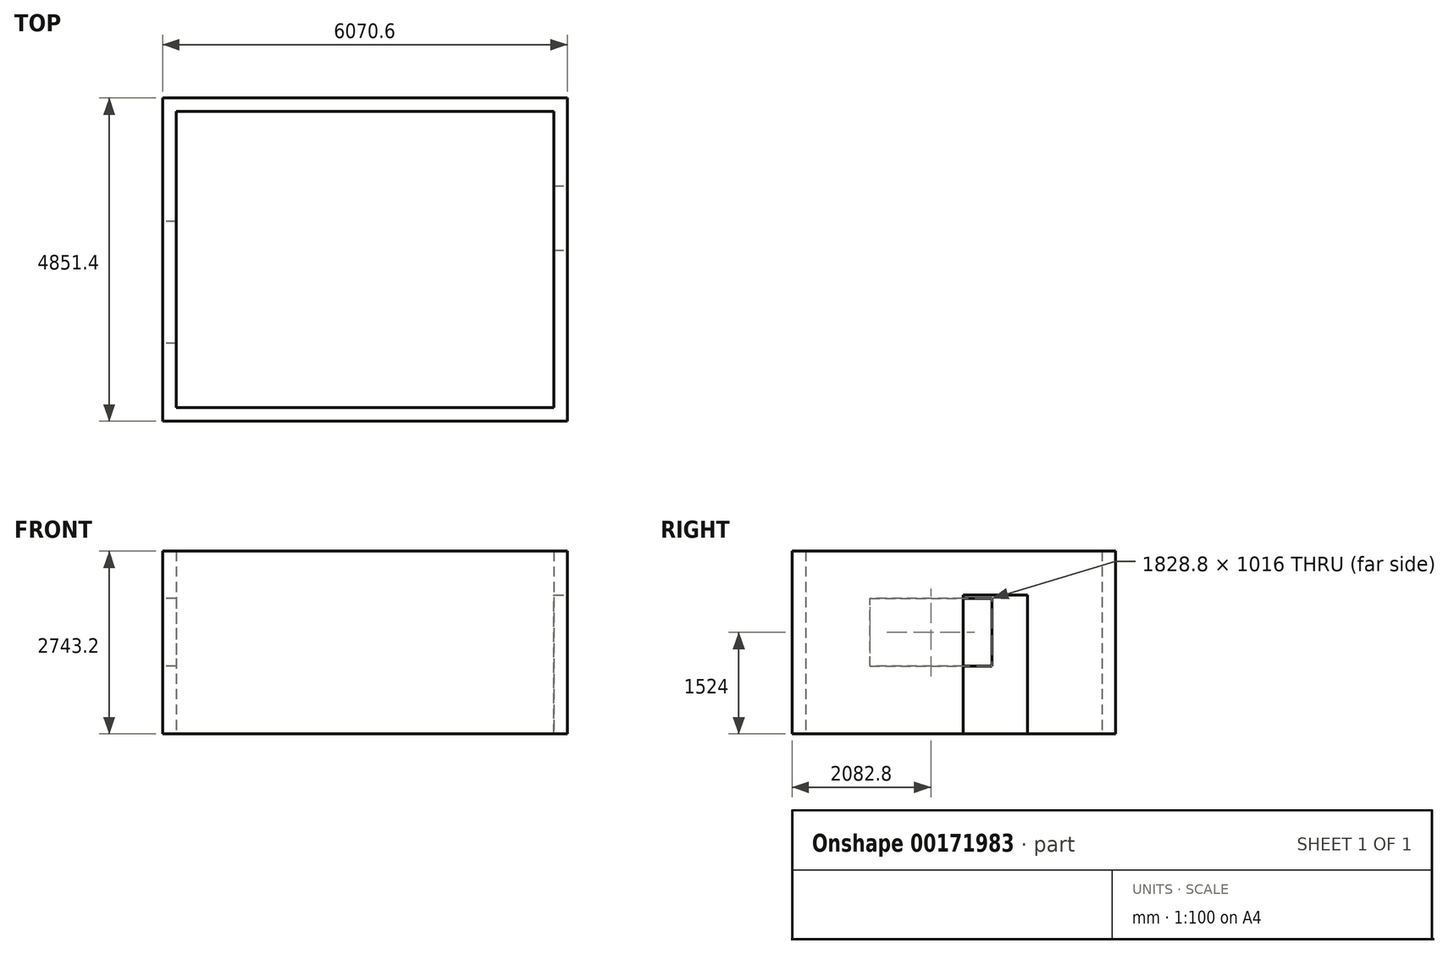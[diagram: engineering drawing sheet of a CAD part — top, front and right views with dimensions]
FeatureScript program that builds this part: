
annotation { "Feature Type Name" : "Feature", "Feature Type Description" : "" }
export const myFeature = defineFeature(function(context is Context, id is Id, definition is map)
    precondition{}
    {
        {
            var Q0;
            Q0=qCreatedBy(makeId("Top.planeOp"),FACE);
            var sketch = newSketch(context, id + "F0", { "sketchPlane" : qUnion([Q0])});
            skLineSegment(sketch, "E0.bottom", {"start": v(3035.3, 2425.7) * mm, "end": v(-3035.3, 2425.7) * mm});
            skLineSegment(sketch, "E0.top", {"start": v(3035.3, -2425.7) * mm, "end": v(-3035.3, -2425.7) * mm});
            skLineSegment(sketch, "E0.left", {"start": v(3035.3, 2425.7) * mm, "end": v(3035.3, -2425.7) * mm});
            skLineSegment(sketch, "E0.right", {"start": v(-3035.3, 2425.7) * mm, "end": v(-3035.3, -2425.7) * mm});
            skPoint(sketch, "E0.middle", {"position": v(0, 0) * mm});
            skLineSegment(sketch, "E1.bottom", {"start": v(2832.1, 2222.5) * mm, "end": v(-2832.1, 2222.5) * mm});
            skLineSegment(sketch, "E1.top", {"start": v(2832.1, -2222.5) * mm, "end": v(-2832.1, -2222.5) * mm});
            skLineSegment(sketch, "E1.left", {"start": v(2832.1, 2222.5) * mm, "end": v(2832.1, -2222.5) * mm});
            skLineSegment(sketch, "E1.right", {"start": v(-2832.1, 2222.5) * mm, "end": v(-2832.1, -2222.5) * mm});
            skSolve(sketch);
        }
        {
            var Q0;
            Q0 = qSketchRegion(id + "F0", true);
            extrude(context, id + "F1", {"entities" : qUnion([Q0]), "depth" : 2438.4 * mm});
        }
        {
            var Q0;
            Q0=makeQuery(id+"F1.opExtrude","SWEPT_FACE",FACE,{"disambiguationData":[OSD([sQuery(id+"F0.wireOp",EDGE,"E0.right")])]});
            var sketch = newSketch(context, id + "F2", { "sketchPlane" : qUnion([Q0])});
            skLineSegment(sketch, "E2.bottom", {"start": v(1257.3, 1016) * mm, "end": v(-571.5, 1016) * mm});
            skLineSegment(sketch, "E2.top", {"start": v(1257.3, 2032) * mm, "end": v(-571.5, 2032) * mm});
            skLineSegment(sketch, "E2.left", {"start": v(1257.3, 1016) * mm, "end": v(1257.3, 2032) * mm});
            skLineSegment(sketch, "E2.right", {"start": v(-571.5, 1016) * mm, "end": v(-571.5, 2032) * mm});
            skSolve(sketch);
        }
        {
            var Q0;
            Q0 = qSketchRegion(id + "F2", true);
            extrude(context, id + "F3", {"entities" : qUnion([Q0]), "operationType" : NewBodyOperationType.REMOVE, "oppositeDirection" : true, "depth" : 254 * mm});
        }
        {
            var Q0;
            Q0=makeQuery(id+"F1.opExtrude","SWEPT_FACE",FACE,{"disambiguationData":[OSD([sQuery(id+"F0.wireOp",EDGE,"E0.left")])]});
            var sketch = newSketch(context, id + "F4", { "sketchPlane" : qUnion([Q0])});
            skLineSegment(sketch, "E3.bottom", {"start": v(1104.9, 0) * mm, "end": v(139.7, 0) * mm});
            skLineSegment(sketch, "E3.top", {"start": v(1104.9, 2082.8) * mm, "end": v(139.7, 2082.8) * mm});
            skLineSegment(sketch, "E3.left", {"start": v(1104.9, 0) * mm, "end": v(1104.9, 2082.8) * mm});
            skLineSegment(sketch, "E3.right", {"start": v(139.7, 0) * mm, "end": v(139.7, 2082.8) * mm});
            skSolve(sketch);
        }
        {
            var Q0;
            Q0 = qSketchRegion(id + "F4", true);
            extrude(context, id + "F5", {"entities" : qUnion([Q0]), "operationType" : NewBodyOperationType.REMOVE, "oppositeDirection" : true, "depth" : 254 * mm});
        }
        {
            var Q0;
            Q0=makeQuery(id+"F1.opExtrude","CAP_FACE",FACE,{"disambiguationData":[OSD([sQuery(id+"F0.wireOp",EDGE,"E0.bottom"),sQuery(id+"F0.wireOp",EDGE,"E0.top"),sQuery(id+"F0.wireOp",EDGE,"E0.left"),sQuery(id+"F0.wireOp",EDGE,"E0.right"),sQuery(id+"F0.wireOp",EDGE,"E1.bottom"),sQuery(id+"F0.wireOp",EDGE,"E1.top"),sQuery(id+"F0.wireOp",EDGE,"E1.left"),sQuery(id+"F0.wireOp",EDGE,"E1.right")])],"isStart":false});
            extrude(context, id + "F6", {"entities" : qUnion([Q0]), "operationType" : NewBodyOperationType.ADD, "depth" : 304.8 * mm});
        }
    });
